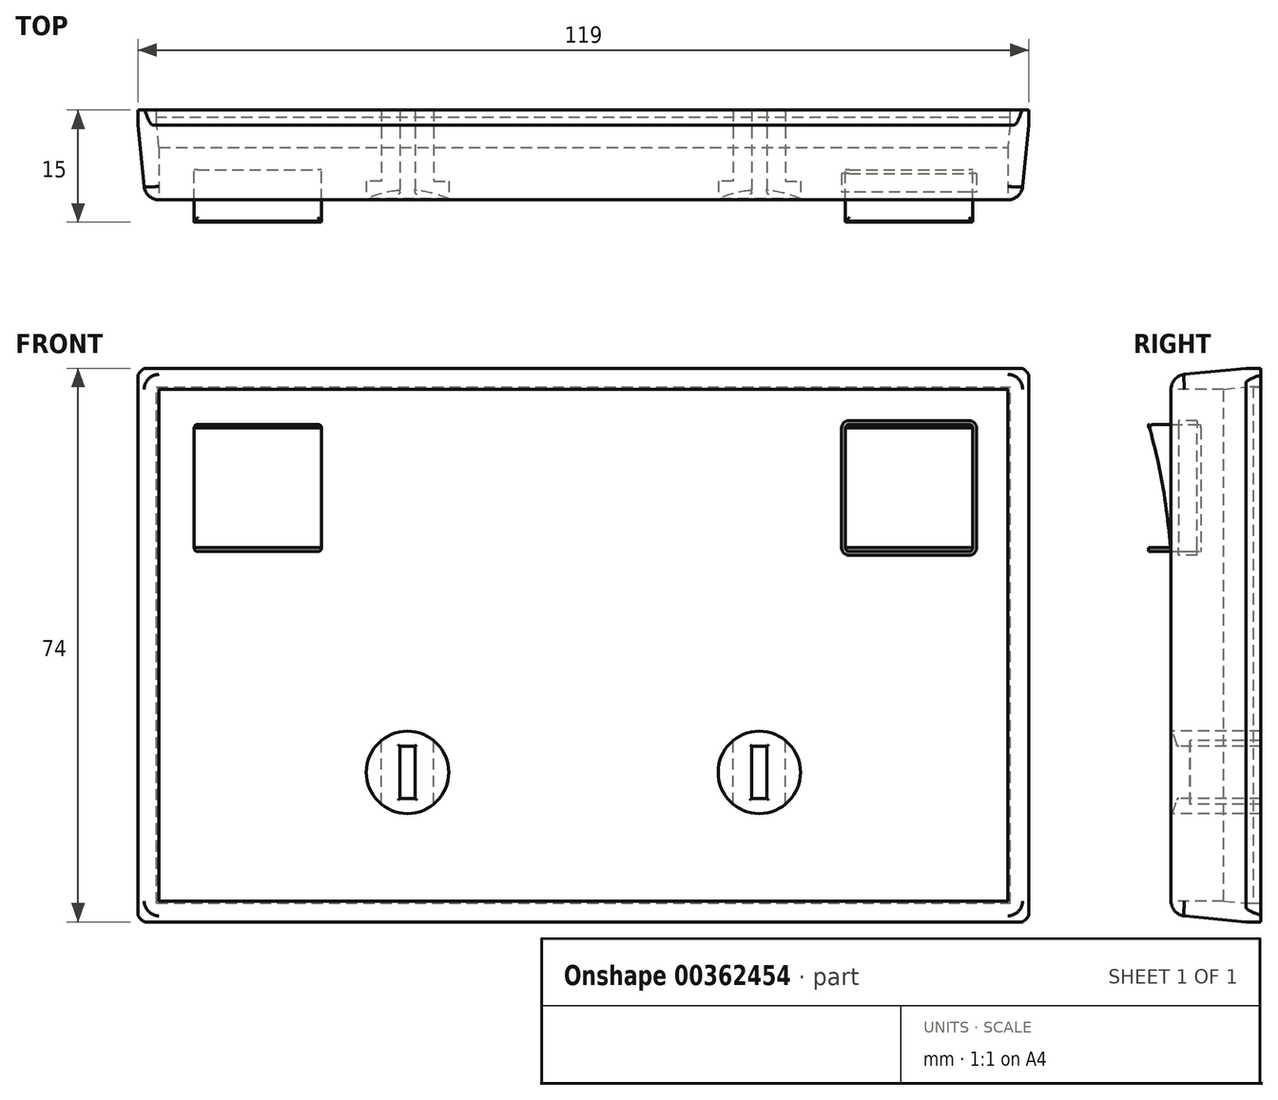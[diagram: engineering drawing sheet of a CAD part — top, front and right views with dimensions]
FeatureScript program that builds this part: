
annotation { "Feature Type Name" : "Feature", "Feature Type Description" : "" }
export const myFeature = defineFeature(function(context is Context, id is Id, definition is map)
    precondition{}
    {
        {
            var Q0;
            Q0=qCreatedBy(makeId("Front.planeOp"),FACE);
            var sketch = newSketch(context, id + "F0", { "sketchPlane" : qUnion([Q0])});
            skLineSegment(sketch, "E0.bottom", {"start": v(59.5, 37) * mm, "end": v(-59.5, 37) * mm});
            skLineSegment(sketch, "E0.top", {"start": v(59.5, -37) * mm, "end": v(-59.5, -37) * mm});
            skLineSegment(sketch, "E0.left", {"start": v(59.5, 37) * mm, "end": v(59.5, -37) * mm});
            skLineSegment(sketch, "E0.right", {"start": v(-59.5, 37) * mm, "end": v(-59.5, -37) * mm});
            skPoint(sketch, "E0.middle", {"position": v(0, 0) * mm});
            skSolve(sketch);
        }
        {
            var Q0;
            Q0=makeQuery(id+"F0.imprint","IMPRINT",FACE,{"disambiguationData":[TD([[makeQuery(id+"F0.imprint","IMPRINT",EDGE,{"derivedFrom":sQuery(id+"F0.wireOp",EDGE,"E0.bottom")}),1.0]])]});
            extrude(context, id + "F1", {"entities" : qUnion([Q0]), "depth" : 12 * mm});
        }
        {
            var Q0;
            Q0=makeQuery(id+"F1.opExtrude","CAP_EDGE",EDGE,{"disambiguationData":[OSD([sQuery(id+"F0.wireOp",EDGE,"E0.right")])],"isStart":false});
            var Q1;
            Q1=makeQuery(id+"F1.opExtrude","CAP_EDGE",EDGE,{"disambiguationData":[OSD([sQuery(id+"F0.wireOp",EDGE,"E0.bottom")])],"isStart":false});
            var Q2;
            Q2=makeQuery(id+"F1.opExtrude","CAP_EDGE",EDGE,{"disambiguationData":[OSD([sQuery(id+"F0.wireOp",EDGE,"E0.left")])],"isStart":false});
            var Q3;
            Q3=makeQuery(id+"F1.opExtrude","CAP_EDGE",EDGE,{"disambiguationData":[OSD([sQuery(id+"F0.wireOp",EDGE,"E0.top")])],"isStart":false});
            chamfer(context, id + "F2", {"entities" : qUnion([Q0, Q1, Q2, Q3]), "chamferType" : ChamferType.TWO_OFFSETS, "width1" : 1 * mm, "oppositeDirection" : false, "width2" : 10 * mm, "tangentPropagation" : true});
        }
        {
            var Q0;
            {var subQ0=sQuery(id+"F0.wireOp",EDGE,"E0.right");Q0=makeQuery(id+"F2.opChamfer","BLEND_EDGE",EDGE,{"blendedFrom":[makeQuery(id+"F1.opExtrude","CAP_EDGE",EDGE,{"disambiguationData":[OSD([subQ0])],"isStart":false}),makeQuery(id+"F1.opExtrude","CAP_FACE",FACE,{"disambiguationData":[OSD([sQuery(id+"F0.wireOp",EDGE,"E0.bottom"),sQuery(id+"F0.wireOp",EDGE,"E0.top"),sQuery(id+"F0.wireOp",EDGE,"E0.left"),subQ0])],"isStart":false})],"blendedInto":[makeQuery(id+"F1.opExtrude","CAP_FACE",FACE,{"disambiguationData":[OSD([sQuery(id+"F0.wireOp",EDGE,"E0.bottom"),sQuery(id+"F0.wireOp",EDGE,"E0.top"),sQuery(id+"F0.wireOp",EDGE,"E0.left"),subQ0])],"isStart":false})]});}
            var Q1;
            {var subQ0=sQuery(id+"F0.wireOp",EDGE,"E0.bottom");Q1=makeQuery(id+"F2.opChamfer","BLEND_EDGE",EDGE,{"blendedFrom":[makeQuery(id+"F1.opExtrude","CAP_EDGE",EDGE,{"disambiguationData":[OSD([subQ0])],"isStart":false}),makeQuery(id+"F1.opExtrude","CAP_FACE",FACE,{"disambiguationData":[OSD([subQ0,sQuery(id+"F0.wireOp",EDGE,"E0.top"),sQuery(id+"F0.wireOp",EDGE,"E0.left"),sQuery(id+"F0.wireOp",EDGE,"E0.right")])],"isStart":false})],"blendedInto":[makeQuery(id+"F1.opExtrude","CAP_FACE",FACE,{"disambiguationData":[OSD([subQ0,sQuery(id+"F0.wireOp",EDGE,"E0.top"),sQuery(id+"F0.wireOp",EDGE,"E0.left"),sQuery(id+"F0.wireOp",EDGE,"E0.right")])],"isStart":false})]});}
            var Q2;
            {var subQ0=sQuery(id+"F0.wireOp",EDGE,"E0.top");Q2=makeQuery(id+"F2.opChamfer","BLEND_EDGE",EDGE,{"blendedFrom":[makeQuery(id+"F1.opExtrude","CAP_EDGE",EDGE,{"disambiguationData":[OSD([subQ0])],"isStart":false}),makeQuery(id+"F1.opExtrude","CAP_FACE",FACE,{"disambiguationData":[OSD([sQuery(id+"F0.wireOp",EDGE,"E0.bottom"),subQ0,sQuery(id+"F0.wireOp",EDGE,"E0.left"),sQuery(id+"F0.wireOp",EDGE,"E0.right")])],"isStart":false})],"blendedInto":[makeQuery(id+"F1.opExtrude","CAP_FACE",FACE,{"disambiguationData":[OSD([sQuery(id+"F0.wireOp",EDGE,"E0.bottom"),subQ0,sQuery(id+"F0.wireOp",EDGE,"E0.left"),sQuery(id+"F0.wireOp",EDGE,"E0.right")])],"isStart":false})]});}
            var Q3;
            {var subQ0=sQuery(id+"F0.wireOp",EDGE,"E0.left");Q3=makeQuery(id+"F2.opChamfer","BLEND_EDGE",EDGE,{"blendedFrom":[makeQuery(id+"F1.opExtrude","CAP_EDGE",EDGE,{"disambiguationData":[OSD([subQ0])],"isStart":false}),makeQuery(id+"F1.opExtrude","CAP_FACE",FACE,{"disambiguationData":[OSD([sQuery(id+"F0.wireOp",EDGE,"E0.bottom"),sQuery(id+"F0.wireOp",EDGE,"E0.top"),subQ0,sQuery(id+"F0.wireOp",EDGE,"E0.right")])],"isStart":false})],"blendedInto":[makeQuery(id+"F1.opExtrude","CAP_FACE",FACE,{"disambiguationData":[OSD([sQuery(id+"F0.wireOp",EDGE,"E0.bottom"),sQuery(id+"F0.wireOp",EDGE,"E0.top"),subQ0,sQuery(id+"F0.wireOp",EDGE,"E0.right")])],"isStart":false})]});}
            fillet(context, id + "F3", {"entities" : qUnion([Q0, Q1, Q2, Q3]), "radius" : 2 * mm, "tangentPropagation" : true, "allowEdgeOverflow" : false});
        }
        {
            var Q0;
            Q0=makeQuery(id+"F2.opChamfer","BLEND_EDGE",EDGE,{"blendedFrom":[makeQuery(id+"F1.opExtrude","CAP_EDGE",EDGE,{"disambiguationData":[OSD([sQuery(id+"F0.wireOp",EDGE,"E0.bottom")])],"isStart":false}),makeQuery(id+"F1.opExtrude","CAP_EDGE",EDGE,{"disambiguationData":[OSD([sQuery(id+"F0.wireOp",EDGE,"E0.right")])],"isStart":false})],"blendedInto":[]});
            var Q1;
            Q1=makeQuery(id+"F2.opChamfer","BLEND_EDGE",EDGE,{"blendedFrom":[makeQuery(id+"F1.opExtrude","CAP_EDGE",EDGE,{"disambiguationData":[OSD([sQuery(id+"F0.wireOp",EDGE,"E0.top")])],"isStart":false}),makeQuery(id+"F1.opExtrude","CAP_EDGE",EDGE,{"disambiguationData":[OSD([sQuery(id+"F0.wireOp",EDGE,"E0.right")])],"isStart":false})],"blendedInto":[]});
            var Q2;
            Q2=makeQuery(id+"F2.opChamfer","BLEND_EDGE",EDGE,{"blendedFrom":[makeQuery(id+"F1.opExtrude","CAP_EDGE",EDGE,{"disambiguationData":[OSD([sQuery(id+"F0.wireOp",EDGE,"E0.top")])],"isStart":false}),makeQuery(id+"F1.opExtrude","CAP_EDGE",EDGE,{"disambiguationData":[OSD([sQuery(id+"F0.wireOp",EDGE,"E0.left")])],"isStart":false})],"blendedInto":[]});
            var Q3;
            Q3=makeQuery(id+"F2.opChamfer","BLEND_EDGE",EDGE,{"blendedFrom":[makeQuery(id+"F1.opExtrude","CAP_EDGE",EDGE,{"disambiguationData":[OSD([sQuery(id+"F0.wireOp",EDGE,"E0.bottom")])],"isStart":false}),makeQuery(id+"F1.opExtrude","CAP_EDGE",EDGE,{"disambiguationData":[OSD([sQuery(id+"F0.wireOp",EDGE,"E0.left")])],"isStart":false})],"blendedInto":[]});
            fillet(context, id + "F4", {"entities" : qUnion([Q0, Q1, Q2, Q3]), "radius" : 2 * mm, "tangentPropagation" : true, "allowEdgeOverflow" : false});
        }
        {
            var Q0;
            Q0=makeQuery(id+"F1.opExtrude","CAP_FACE",FACE,{"disambiguationData":[OSD([sQuery(id+"F0.wireOp",EDGE,"E0.bottom"),sQuery(id+"F0.wireOp",EDGE,"E0.top"),sQuery(id+"F0.wireOp",EDGE,"E0.left"),sQuery(id+"F0.wireOp",EDGE,"E0.right")])],"isStart":false});
            var sketch = newSketch(context, id + "F5", { "sketchPlane" : qUnion([Q0])});
            skLineSegment(sketch, "E1", {"start": v(0, 34.2) * mm, "end": v(0, -34.2) * mm, "construction": true});
            skLineSegment(sketch, "E2", {"start": v(-23.5, 34.2) * mm, "end": v(-23.5, -34.2) * mm, "construction": true});
            skPoint(sketch, "E3", {"position": v(-23.5, -17) * mm});
            skCircle(sketch, "E4", {"center": v(-23.5, -17) * mm, "radius": 5.5 * mm});
            skLineSegment(sketch, "E5.bottom", {"start": v(-22.5, -13.5) * mm, "end": v(-24.5, -13.5) * mm});
            skLineSegment(sketch, "E5.top", {"start": v(-22.5, -20.5) * mm, "end": v(-24.5, -20.5) * mm});
            skLineSegment(sketch, "E5.left", {"start": v(-22.5, -13.5) * mm, "end": v(-22.5, -20.5) * mm});
            skLineSegment(sketch, "E5.right", {"start": v(-24.5, -13.5) * mm, "end": v(-24.5, -20.5) * mm});
            skLineSegment(sketch, "E6", {"start": v(-56.7, -7.5) * mm, "end": v(56.7, -7.5) * mm, "construction": true});
            skPoint(sketch, "E7", {"position": v(-33.5, -7.5) * mm});
            skPoint(sketch, "E8", {"position": v(-13.5, -7.5) * mm});
            skLineSegment(sketch, "E9", {"start": v(-30, -34.2) * mm, "end": v(-30, 34.2) * mm, "construction": true});
            skLineSegment(sketch, "E10", {"start": v(-33.5, -7.5) * mm, "end": v(-30, -1.44) * mm});
            skLineSegment(sketch, "E11", {"start": v(-30, -1.44) * mm, "end": v(-28.27, -2.44) * mm});
            skLineSegment(sketch, "E12", {"start": v(-28.27, -2.44) * mm, "end": v(-31.77, -8.5) * mm});
            skLineSegment(sketch, "E13", {"start": v(-31.77, -8.5) * mm, "end": v(-33.5, -7.5) * mm});
            skLineSegment(sketch, "E14.MirrorCS", {"start": v(-15.23, -8.5) * mm, "end": v(-13.5, -7.5) * mm});
            skLineSegment(sketch, "E15.MirrorCS", {"start": v(-18.73, -2.44) * mm, "end": v(-15.23, -8.5) * mm});
            skLineSegment(sketch, "E16.MirrorCS", {"start": v(-13.5, -7.5) * mm, "end": v(-17, -1.44) * mm});
            skLineSegment(sketch, "E17.MirrorCS", {"start": v(-17, -1.44) * mm, "end": v(-18.73, -2.44) * mm});
            skCircle(sketch, "E18.MirrorC", {"center": v(23.5, -17) * mm, "radius": 5.5 * mm});
            skLineSegment(sketch, "E19.MirrorCS", {"start": v(22.5, -20.5) * mm, "end": v(24.5, -20.5) * mm});
            skLineSegment(sketch, "E20.MirrorCS", {"start": v(24.5, -13.5) * mm, "end": v(24.5, -20.5) * mm});
            skLineSegment(sketch, "E21.MirrorCS", {"start": v(22.5, -13.5) * mm, "end": v(24.5, -13.5) * mm});
            skLineSegment(sketch, "E22.MirrorCS", {"start": v(22.5, -13.5) * mm, "end": v(22.5, -20.5) * mm});
            skLineSegment(sketch, "E23.MirrorCS", {"start": v(15.23, -8.5) * mm, "end": v(13.5, -7.5) * mm});
            skLineSegment(sketch, "E24.MirrorCS", {"start": v(13.5, -7.5) * mm, "end": v(17, -1.44) * mm});
            skLineSegment(sketch, "E25.MirrorCS", {"start": v(17, -1.44) * mm, "end": v(18.73, -2.44) * mm});
            skLineSegment(sketch, "E26.MirrorCS", {"start": v(18.73, -2.44) * mm, "end": v(15.23, -8.5) * mm});
            skLineSegment(sketch, "E27.MirrorCS", {"start": v(31.77, -8.5) * mm, "end": v(33.5, -7.5) * mm});
            skLineSegment(sketch, "E28.MirrorCS", {"start": v(30, -1.44) * mm, "end": v(28.27, -2.44) * mm});
            skLineSegment(sketch, "E29.MirrorCS", {"start": v(33.5, -7.5) * mm, "end": v(30, -1.44) * mm});
            skLineSegment(sketch, "E30.MirrorCS", {"start": v(28.27, -2.44) * mm, "end": v(31.77, -8.5) * mm});
            skSolve(sketch);
        }
        {
            var Q0;
            Q0=makeQuery(id+"F5.imprint","IMPRINT",FACE,{"disambiguationData":[TD([[makeQuery(id+"F5.imprint","IMPRINT",EDGE,{"derivedFrom":sQuery(id+"F5.wireOp",EDGE,"E10")}),-1.0]])]});
            var Q1;
            Q1=makeQuery(id+"F5.imprint","IMPRINT",FACE,{"disambiguationData":[TD([[makeQuery(id+"F5.imprint","IMPRINT",EDGE,{"derivedFrom":sQuery(id+"F5.wireOp",EDGE,"E14.MirrorCS")}),1.0]])]});
            var Q2;
            Q2=makeQuery(id+"F5.imprint","IMPRINT",FACE,{"disambiguationData":[TD([[makeQuery(id+"F5.imprint","IMPRINT",EDGE,{"derivedFrom":sQuery(id+"F5.wireOp",EDGE,"E5.bottom")}),1.0]])]});
            var Q3;
            Q3=makeQuery(id+"F5.imprint","IMPRINT",FACE,{"disambiguationData":[TD([[makeQuery(id+"F5.imprint","IMPRINT",EDGE,{"derivedFrom":sQuery(id+"F5.wireOp",EDGE,"E23.MirrorCS")}),-1.0]])]});
            var Q4;
            Q4=makeQuery(id+"F5.imprint","IMPRINT",FACE,{"disambiguationData":[TD([[makeQuery(id+"F5.imprint","IMPRINT",EDGE,{"derivedFrom":sQuery(id+"F5.wireOp",EDGE,"E27.MirrorCS")}),1.0]])]});
            var Q5;
            Q5=makeQuery(id+"F5.imprint","IMPRINT",FACE,{"disambiguationData":[TD([[makeQuery(id+"F5.imprint","IMPRINT",EDGE,{"derivedFrom":sQuery(id+"F5.wireOp",EDGE,"E19.MirrorCS")}),1.0]])]});
            extrude(context, id + "F6", {"entities" : qUnion([Q0, Q1, Q2, Q3, Q4, Q5]), "operationType" : NewBodyOperationType.REMOVE, "endBound" : BoundingType.UP_TO_NEXT, "oppositeDirection" : true, "depth" : 25 * mm});
        }
        {
            var Q0;
            Q0=makeQuery(id+"F1.opExtrude","CAP_FACE",FACE,{"disambiguationData":[OSD([sQuery(id+"F0.wireOp",EDGE,"E0.bottom"),sQuery(id+"F0.wireOp",EDGE,"E0.top"),sQuery(id+"F0.wireOp",EDGE,"E0.left"),sQuery(id+"F0.wireOp",EDGE,"E0.right")])],"isStart":false});
            var sketch = newSketch(context, id + "F7", { "sketchPlane" : qUnion([Q0])});
            skLineSegment(sketch, "E31", {"start": v(-56.7, -10.5) * mm, "end": v(0, -10.5) * mm, "construction": true});
            skLineSegment(sketch, "E32.0", {"start": v(-23.5, 34.2) * mm, "end": v(-23.5, -34.2) * mm});
            skLineSegment(sketch, "E33.bottom", {"start": v(-11, 4.5) * mm, "end": v(-36, 4.5) * mm});
            skLineSegment(sketch, "E33.top", {"start": v(-11, -25.5) * mm, "end": v(-36, -25.5) * mm});
            skLineSegment(sketch, "E33.left", {"start": v(-8.5, 2) * mm, "end": v(-8.5, -23) * mm});
            skLineSegment(sketch, "E33.right", {"start": v(-38.5, 2) * mm, "end": v(-38.5, -23) * mm});
            skPoint(sketch, "E33.middle", {"position": v(-23.5, -10.5) * mm});
            skPoint(sketch, "E34.visualSharp", {"position": v(-38.5, 4.5) * mm});
            skArc(sketch, "E34.filletArc", {"start": v(-36, 4.5) * mm, "mid": v(-37.77, 3.77) * mm, "end": v(-38.5, 2) * mm});
            skPoint(sketch, "E35.visualSharp", {"position": v(-8.5, 4.5) * mm});
            skArc(sketch, "E35.filletArc", {"start": v(-8.5, 2) * mm, "mid": v(-9.23, 3.77) * mm, "end": v(-11, 4.5) * mm});
            skPoint(sketch, "E36.visualSharp", {"position": v(-8.5, -25.5) * mm});
            skArc(sketch, "E36.filletArc", {"start": v(-11, -25.5) * mm, "mid": v(-9.23, -24.77) * mm, "end": v(-8.5, -23) * mm});
            skPoint(sketch, "E37.visualSharp", {"position": v(-38.5, -25.5) * mm});
            skArc(sketch, "E37.filletArc", {"start": v(-38.5, -23) * mm, "mid": v(-37.77, -24.77) * mm, "end": v(-36, -25.5) * mm});
            skLineSegment(sketch, "E38.0", {"start": v(-11.1, 3.5) * mm, "end": v(-35.9, 3.5) * mm});
            skLineSegment(sketch, "E38.1", {"start": v(-9.5, 1.9) * mm, "end": v(-9.5, -22.9) * mm});
            skLineSegment(sketch, "E38.2", {"start": v(-11.1, -24.5) * mm, "end": v(-35.9, -24.5) * mm});
            skLineSegment(sketch, "E38.3", {"start": v(-37.5, 1.9) * mm, "end": v(-37.5, -22.9) * mm});
            skPoint(sketch, "E39.visualSharp", {"position": v(-37.5, 3.5) * mm});
            skArc(sketch, "E39.filletArc", {"start": v(-35.9, 3.5) * mm, "mid": v(-37.03, 3.03) * mm, "end": v(-37.5, 1.9) * mm});
            skPoint(sketch, "E40.visualSharp", {"position": v(-9.5, 3.5) * mm});
            skArc(sketch, "E40.filletArc", {"start": v(-9.5, 1.9) * mm, "mid": v(-9.97, 3.03) * mm, "end": v(-11.1, 3.5) * mm});
            skPoint(sketch, "E41.visualSharp", {"position": v(-9.5, -24.5) * mm});
            skArc(sketch, "E41.filletArc", {"start": v(-11.1, -24.5) * mm, "mid": v(-9.97, -24.03) * mm, "end": v(-9.5, -22.9) * mm});
            skPoint(sketch, "E42.visualSharp", {"position": v(-37.5, -24.5) * mm});
            skArc(sketch, "E42.filletArc", {"start": v(-37.5, -22.9) * mm, "mid": v(-37.03, -24.03) * mm, "end": v(-35.9, -24.5) * mm});
            skArc(sketch, "E43.MirrorCS", {"start": v(38.5, -23) * mm, "mid": v(37.77, -24.77) * mm, "end": v(36, -25.5) * mm});
            skArc(sketch, "E44.MirrorCS", {"start": v(37.5, -22.9) * mm, "mid": v(37.03, -24.03) * mm, "end": v(35.9, -24.5) * mm});
            skLineSegment(sketch, "E45.MirrorCS", {"start": v(11, -25.5) * mm, "end": v(36, -25.5) * mm});
            skLineSegment(sketch, "E46.MirrorCS", {"start": v(11.1, -24.5) * mm, "end": v(35.9, -24.5) * mm});
            skArc(sketch, "E47.MirrorCS", {"start": v(11.1, -24.5) * mm, "mid": v(9.97, -24.03) * mm, "end": v(9.5, -22.9) * mm});
            skArc(sketch, "E48.MirrorCS", {"start": v(11, -25.5) * mm, "mid": v(9.23, -24.77) * mm, "end": v(8.5, -23) * mm});
            skLineSegment(sketch, "E49.MirrorCS", {"start": v(8.5, 2) * mm, "end": v(8.5, -23) * mm});
            skLineSegment(sketch, "E50.MirrorCS", {"start": v(9.5, 1.9) * mm, "end": v(9.5, -22.9) * mm});
            skArc(sketch, "E51.MirrorCS", {"start": v(9.5, 1.9) * mm, "mid": v(9.97, 3.03) * mm, "end": v(11.1, 3.5) * mm});
            skArc(sketch, "E52.MirrorCS", {"start": v(8.5, 2) * mm, "mid": v(9.23, 3.77) * mm, "end": v(11, 4.5) * mm});
            skLineSegment(sketch, "E53.MirrorCS", {"start": v(37.5, 1.9) * mm, "end": v(37.5, -22.9) * mm});
            skLineSegment(sketch, "E54.MirrorCS", {"start": v(38.5, 2) * mm, "end": v(38.5, -23) * mm});
            skArc(sketch, "E55.MirrorCS", {"start": v(35.9, 3.5) * mm, "mid": v(37.03, 3.03) * mm, "end": v(37.5, 1.9) * mm});
            skArc(sketch, "E56.MirrorCS", {"start": v(36, 4.5) * mm, "mid": v(37.77, 3.77) * mm, "end": v(38.5, 2) * mm});
            skLineSegment(sketch, "E57.MirrorCS", {"start": v(11, 4.5) * mm, "end": v(36, 4.5) * mm});
            skLineSegment(sketch, "E58.MirrorCS", {"start": v(11.1, 3.5) * mm, "end": v(35.9, 3.5) * mm});
            skSolve(sketch);
        }
        {
            var Q0;
            Q0=makeQuery(id+"F7.imprint","IMPRINT",FACE,{"disambiguationData":[TD([[makeQuery(id+"F7.imprint","IMPRINT",EDGE,{"derivedFrom":sQuery(id+"F7.wireOp",EDGE,"E33.right")}),1.0]])]});
            var Q1;
            Q1=makeQuery(id+"F7.imprint","IMPRINT",FACE,{"disambiguationData":[TD([[makeQuery(id+"F7.imprint","IMPRINT",EDGE,{"derivedFrom":sQuery(id+"F7.wireOp",EDGE,"E33.left")}),-1.0]])]});
            var Q2;
            Q2=makeQuery(id+"F7.imprint","IMPRINT",FACE,{"disambiguationData":[TD([[makeQuery(id+"F7.imprint","IMPRINT",EDGE,{"derivedFrom":sQuery(id+"F7.wireOp",EDGE,"E43.MirrorCS")}),-1.0]])]});
            extrude(context, id + "F8", {"entities" : qUnion([Q0, Q1, Q2]), "operationType" : NewBodyOperationType.REMOVE, "oppositeDirection" : true, "depth" : 1 * mm});
        }
        {
            var Q0;
            Q0=makeQuery(id+"F5.imprint","IMPRINT",FACE,{"disambiguationData":[TD([[makeQuery(id+"F5.imprint","IMPRINT",EDGE,{"derivedFrom":sQuery(id+"F5.wireOp",EDGE,"E4")}),-1.0]])]});
            var sketch = newSketch(context, id + "F9", { "sketchPlane" : qUnion([Q0])});
            skLineSegment(sketch, "E59.bottom", {"start": v(-51.5, 30) * mm, "end": v(-35.5, 30) * mm});
            skLineSegment(sketch, "E59.top", {"start": v(-51.5, 12) * mm, "end": v(-35.5, 12) * mm});
            skLineSegment(sketch, "E59.left", {"start": v(-52.5, 29) * mm, "end": v(-52.5, 13) * mm});
            skLineSegment(sketch, "E59.right", {"start": v(-34.5, 29) * mm, "end": v(-34.5, 13) * mm});
            skPoint(sketch, "E60.visualSharp", {"position": v(-52.5, 30) * mm});
            skArc(sketch, "E60.filletArc", {"start": v(-51.5, 30) * mm, "mid": v(-52.2, 29.7) * mm, "end": v(-52.5, 29) * mm});
            skPoint(sketch, "E61.visualSharp", {"position": v(-34.5, 30) * mm});
            skArc(sketch, "E61.filletArc", {"start": v(-34.5, 29) * mm, "mid": v(-34.8, 29.7) * mm, "end": v(-35.5, 30) * mm});
            skPoint(sketch, "E62.visualSharp", {"position": v(-34.5, 12) * mm});
            skArc(sketch, "E62.filletArc", {"start": v(-35.5, 12) * mm, "mid": v(-34.8, 12.3) * mm, "end": v(-34.5, 13) * mm});
            skPoint(sketch, "E63.visualSharp", {"position": v(-52.5, 12) * mm});
            skArc(sketch, "E63.filletArc", {"start": v(-52.5, 13) * mm, "mid": v(-52.2, 12.3) * mm, "end": v(-51.5, 12) * mm});
            skArc(sketch, "E64.MirrorCS", {"start": v(34.5, 29) * mm, "mid": v(34.8, 29.7) * mm, "end": v(35.5, 30) * mm});
            skLineSegment(sketch, "E65.MirrorCS", {"start": v(34.5, 29) * mm, "end": v(34.5, 13) * mm});
            skArc(sketch, "E66.MirrorCS", {"start": v(35.5, 12) * mm, "mid": v(34.8, 12.3) * mm, "end": v(34.5, 13) * mm});
            skLineSegment(sketch, "E67.MirrorCS", {"start": v(51.5, 12) * mm, "end": v(35.5, 12) * mm});
            skArc(sketch, "E68.MirrorCS", {"start": v(52.5, 13) * mm, "mid": v(52.2, 12.3) * mm, "end": v(51.5, 12) * mm});
            skLineSegment(sketch, "E69.MirrorCS", {"start": v(51.5, 30) * mm, "end": v(35.5, 30) * mm});
            skLineSegment(sketch, "E70.MirrorCS", {"start": v(52.5, 29) * mm, "end": v(52.5, 13) * mm});
            skArc(sketch, "E71.MirrorCS", {"start": v(51.5, 30) * mm, "mid": v(52.2, 29.7) * mm, "end": v(52.5, 29) * mm});
            skSolve(sketch);
        }
        {
            var Q0;
            Q0=makeQuery(id+"F9.imprint","IMPRINT",FACE,{"disambiguationData":[TD([[makeQuery(id+"F9.imprint","IMPRINT",EDGE,{"derivedFrom":sQuery(id+"F9.wireOp",EDGE,"E59.bottom")}),-1.0]])]});
            extrude(context, id + "F10", {"entities" : qUnion([Q0]), "operationType" : NewBodyOperationType.REMOVE, "endBound" : BoundingType.UP_TO_NEXT, "oppositeDirection" : true, "depth" : 25 * mm});
        }
        {
            var Q0;
            Q0=makeQuery(id+"F1.opExtrude","CAP_FACE",FACE,{"disambiguationData":[OSD([sQuery(id+"F0.wireOp",EDGE,"E0.bottom"),sQuery(id+"F0.wireOp",EDGE,"E0.top"),sQuery(id+"F0.wireOp",EDGE,"E0.left"),sQuery(id+"F0.wireOp",EDGE,"E0.right")])],"isStart":true});
            shell(context, id + "F11", {"entities" : qUnion([Q0]), "thickness" : 2.5 * mm});
        }
        {
            var Q0;
            Q0=makeQuery(id+"F5.imprint","IMPRINT",FACE,{"disambiguationData":[TD([[makeQuery(id+"F5.imprint","IMPRINT",EDGE,{"derivedFrom":sQuery(id+"F5.wireOp",EDGE,"E4")}),-1.0]])]});
            var sketch = newSketch(context, id + "F12", { "sketchPlane" : qUnion([Q0])});
            skLineSegment(sketch, "E72.0", {"start": v(-51.5, 30) * mm, "end": v(-35.5, 30) * mm});
            skLineSegment(sketch, "E73.0", {"start": v(-34.5, 29) * mm, "end": v(-34.5, 13) * mm});
            skLineSegment(sketch, "E74.0", {"start": v(-51.5, 12) * mm, "end": v(-35.5, 12) * mm});
            skLineSegment(sketch, "E75.0", {"start": v(-52.5, 29) * mm, "end": v(-52.5, 13) * mm});
            skLineSegment(sketch, "E76.0", {"start": v(-51.5, 29.5) * mm, "end": v(-35.5, 29.5) * mm});
            skLineSegment(sketch, "E77.0", {"start": v(-52, 29) * mm, "end": v(-52, 13) * mm});
            skLineSegment(sketch, "E78.0", {"start": v(-51.5, 12.5) * mm, "end": v(-35.5, 12.5) * mm});
            skLineSegment(sketch, "E79.0", {"start": v(-35, 29) * mm, "end": v(-35, 13) * mm});
            skArc(sketch, "E80.filletArc", {"start": v(-51.5, 29.5) * mm, "mid": v(-51.85, 29.35) * mm, "end": v(-52, 29) * mm});
            skArc(sketch, "E81.filletArc", {"start": v(-35, 29) * mm, "mid": v(-35.15, 29.35) * mm, "end": v(-35.5, 29.5) * mm});
            skArc(sketch, "E82.filletArc", {"start": v(-35.5, 12.5) * mm, "mid": v(-35.15, 12.65) * mm, "end": v(-35, 13) * mm});
            skArc(sketch, "E83.filletArc", {"start": v(-52, 13) * mm, "mid": v(-51.85, 12.65) * mm, "end": v(-51.5, 12.5) * mm});
            skSolve(sketch);
        }
        {
            var Q0;
            Q0=makeQuery(id+"F12.imprint","IMPRINT",FACE,{"disambiguationData":[TD([[makeQuery(id+"F12.imprint","IMPRINT",EDGE,{"derivedFrom":sQuery(id+"F12.wireOp",EDGE,"E76.0")}),-1.0]])]});
            extrude(context, id + "F13", {"entities" : qUnion([Q0]), "depth" : 3 * mm, "hasSecondDirection" : true, "secondDirectionOppositeDirection" : true, "secondDirectionDepth" : 4 * mm});
        }
        {
            var Q0;
            Q0=makeQuery(id+"F13.opExtrude","SWEPT_FACE",FACE,{"disambiguationData":[OSD([sQuery(id+"F12.wireOp",EDGE,"E77.0")])]});
            var sketch = newSketch(context, id + "F14", { "sketchPlane" : qUnion([Q0])});
            skLineSegment(sketch, "E84.0", {"start": v(14.34, 29.5) * mm, "end": v(8, 29.5) * mm});
            skLineSegment(sketch, "E85.0", {"start": v(15, 12.5) * mm, "end": v(8, 12.5) * mm});
            skFitSpline(sketch, "E86", {"points": [v(15, 29.5) * mm, v(12.06, 12.5) * mm], "startDerivative": vector(-4.71, -17) * mm, "endDerivative": vector(-1.43, -19.4) * mm});
            skArc(sketch, "E87.filletArc", {"start": v(14.83, 28.87) * mm, "mid": v(14.74, 29.3) * mm, "end": v(14.34, 29.5) * mm});
            skLineSegment(sketch, "E88", {"start": v(14.34, 29.5) * mm, "end": v(15, 29.5) * mm});
            skLineSegment(sketch, "E89", {"start": v(15, 29.5) * mm, "end": v(15, 12.5) * mm});
            skLineSegment(sketch, "E90", {"start": v(15, 12.5) * mm, "end": v(12.06, 12.5) * mm});
            skSolve(sketch);
        }
        {
            var Q0;
            {var subQ4=sQuery(id+"F14.wireOp",EDGE,"E87.filletArc");var subQ6=sQuery(id+"F14.wireOp",EDGE,"E86");var subQ7=makeQuery(id+"F14.imprint","INTERSECT",VERTEX,{"derivedFrom":[subQ6,subQ4]});Q0=makeQuery(id+"F14.imprint","IMPRINT",FACE,{"disambiguationData":[TD([[makeQuery(id+"F14.imprint","IMPRINT",EDGE,{"disambiguationData":[TD([[subQ7,-1.0]])],"derivedFrom":subQ6}),1.0]])]});}
            var Q1;
            {var subQ0=sQuery(id+"F14.wireOp",EDGE,"E88");Q1=makeQuery(id+"F14.imprint","IMPRINT",FACE,{"disambiguationData":[TD([[makeQuery(id+"F14.imprint","IMPRINT",EDGE,{"derivedFrom":subQ0}),-1.0]])]});}
            var Q2;
            {var subQ0=sQuery(id+"F14.wireOp",EDGE,"E90");Q2=makeQuery(id+"F14.imprint","IMPRINT",FACE,{"disambiguationData":[TD([[makeQuery(id+"F14.imprint","IMPRINT",EDGE,{"derivedFrom":subQ0}),-1.0]])]});}
            var Q3;
            Q3=makeQuery(id+"F13.opExtrude","SWEPT_FACE",FACE,{"disambiguationData":[OSD([sQuery(id+"F12.wireOp",EDGE,"E79.0")])]});
            extrude(context, id + "F15", {"entities" : qUnion([Q0, Q1, Q2]), "operationType" : NewBodyOperationType.REMOVE, "endBound" : BoundingType.UP_TO_SURFACE, "oppositeDirection" : true, "endBoundEntityFace" : qUnion([Q3]), "depth" : 25 * mm});
        }
        {
            var Q0;
            Q0=makeQuery(id+"F9.imprint","IMPRINT",FACE,{"disambiguationData":[TD([[makeQuery(id+"F9.imprint","IMPRINT",EDGE,{"derivedFrom":sQuery(id+"F9.wireOp",EDGE,"E64.MirrorCS")}),-1.0]])]});
            extrude(context, id + "F16", {"entities" : qUnion([Q0]), "operationType" : NewBodyOperationType.REMOVE, "endBound" : BoundingType.UP_TO_NEXT, "oppositeDirection" : true, "depth" : 25 * mm});
        }
        {
            var Q0;
            Q0=makeQuery(id+"F13.opExtrude","SWEPT_BODY",BODY,{"disambiguationData":[OSD([sQuery(id+"F12.wireOp",EDGE,"E76.0"),sQuery(id+"F12.wireOp",EDGE,"E77.0"),sQuery(id+"F12.wireOp",EDGE,"E78.0"),sQuery(id+"F12.wireOp",EDGE,"E79.0"),sQuery(id+"F12.wireOp",EDGE,"E80.filletArc"),sQuery(id+"F12.wireOp",EDGE,"E81.filletArc"),sQuery(id+"F12.wireOp",EDGE,"E82.filletArc"),sQuery(id+"F12.wireOp",EDGE,"E83.filletArc")])]});
            transform(context, id + "F17", {"entities" : qUnion([Q0]), "transformType" : TransformType.TRANSLATION_3D, "dx" : 87 * mm, "dy" : 0 * mm, "dz" : 0 * mm, "makeCopy" : true});
        }
        {
            var Q0;
            Q0=makeQuery(id+"F5.imprint","IMPRINT",FACE,{"disambiguationData":[TD([[makeQuery(id+"F5.imprint","IMPRINT",EDGE,{"derivedFrom":sQuery(id+"F5.wireOp",EDGE,"E4")}),-1.0]])]});
            cPlane(context, id + "F18", {"entities" : qUnion([Q0]), "cplaneType" : CPlaneType.OFFSET, "offset" : 12.2 * mm, "width" : 150 * mm, "height" : 150 * mm});
        }
        {
            var Q0;
            Q0=qCreatedBy(id+"F18.planeOp",FACE);
            var sketch = newSketch(context, id + "F19", { "sketchPlane" : qUnion([Q0])});
            skPoint(sketch, "E91.0", {"position": v(-23.5, -17) * mm});
            skArc(sketch, "E92.0", {"start": v(-23.5, -11.5) * mm, "mid": v(-29, -17) * mm, "end": v(-23.5, -22.5) * mm});
            skArc(sketch, "E93", {"start": v(-23.5, -3.5) * mm, "mid": v(-37, -17) * mm, "end": v(-23.5, -30.5) * mm});
            skLineSegment(sketch, "E94", {"start": v(-23.5, -17) * mm, "end": v(-23.5, -3.5) * mm});
            skLineSegment(sketch, "E95", {"start": v(-23.5, -17) * mm, "end": v(-23.5, -30.5) * mm});
            skLineSegment(sketch, "E96.MirrorCS", {"start": v(23.5, -17) * mm, "end": v(23.5, -3.5) * mm});
            skLineSegment(sketch, "E97.MirrorCS", {"start": v(23.5, -17) * mm, "end": v(23.5, -30.5) * mm});
            skArc(sketch, "E98.MirrorCS", {"start": v(23.5, -3.5) * mm, "mid": v(37, -17) * mm, "end": v(23.5, -30.5) * mm});
            skSolve(sketch);
        }
        {
            var Q0;
            {var subQ0=sQuery(id+"F19.wireOp",EDGE,"E92.0");Q0=makeQuery(id+"F19.imprint","IMPRINT",FACE,{"disambiguationData":[TD([[makeQuery(id+"F19.imprint","IMPRINT",EDGE,{"derivedFrom":subQ0}),-1.0]])]});}
            var Q1;
            Q1=sQuery(id+"F19.wireOp",EDGE,"E94");
            revolve(context, id + "F20", {"operationType" : NewBodyOperationType.REMOVE, "entities" : qUnion([Q0]), "axis" : qUnion([Q1]), "revolveType" : RevolveType.FULL, "oppositeDirection" : true});
        }
        {
            var Q0;
            Q0=makeQuery(id+"F19.imprint","IMPRINT",FACE,{"disambiguationData":[TD([[makeQuery(id+"F19.imprint","IMPRINT",EDGE,{"derivedFrom":sQuery(id+"F19.wireOp",EDGE,"E96.MirrorCS")}),-1.0]])]});
            var Q1;
            Q1=sQuery(id+"F19.wireOp",EDGE,"E96.MirrorCS");
            revolve(context, id + "F21", {"operationType" : NewBodyOperationType.REMOVE, "entities" : qUnion([Q0]), "axis" : qUnion([Q1]), "revolveType" : RevolveType.FULL, "oppositeDirection" : true});
        }
        {
            var Q0;
            {var subQ0=sQuery(id+"F0.wireOp",EDGE,"E0.right");var subQ1=sQuery(id+"F0.wireOp",EDGE,"E0.left");var subQ2=sQuery(id+"F0.wireOp",EDGE,"E0.top");var subQ3=sQuery(id+"F0.wireOp",EDGE,"E0.bottom");Q0=makeQuery(id+"F11.opShell","OFFSET_FACE",FACE,{"disambiguationData":[OSD([subQ3,subQ2,subQ1,subQ0]),TDD([makeQuery(id+"F1.opExtrude","CAP_FACE",FACE,{"disambiguationData":[OSD([subQ3,subQ2,subQ1,subQ0])],"isStart":true})]),OD(0.0)]});}
            var sketch = newSketch(context, id + "F22", { "sketchPlane" : qUnion([Q0])});
            skLineSegment(sketch, "E99.bottom", {"start": v(-57, 34.5) * mm, "end": v(57, 34.5) * mm});
            skLineSegment(sketch, "E99.top", {"start": v(-57, -34.5) * mm, "end": v(57, -34.5) * mm});
            skLineSegment(sketch, "E99.left", {"start": v(-57, 34.5) * mm, "end": v(-57, -34.5) * mm});
            skLineSegment(sketch, "E99.right", {"start": v(57, 34.5) * mm, "end": v(57, -34.5) * mm});
            skSolve(sketch);
        }
        {
            var Q0;
            Q0=makeQuery(id+"F22.imprint","IMPRINT",FACE,{"disambiguationData":[TD([[makeQuery(id+"F22.imprint","IMPRINT",EDGE,{"derivedFrom":sQuery(id+"F22.wireOp",EDGE,"E99.bottom")}),-1.0]])]});
            extrude(context, id + "F23", {"entities" : qUnion([Q0]), "oppositeDirection" : true, "depth" : 1 * mm});
        }
        {
            var Q0;
            Q0=makeQuery(id+"F6.boolean.opBoolean","COPY",EDGE,{"derivedFrom":makeQuery(id+"F6.opExtrude","CAP_EDGE",EDGE,{"disambiguationData":[OSD([sQuery(id+"F5.wireOp",EDGE,"E10")])],"isStart":true})});
            var Q1;
            Q1=makeQuery(id+"F6.boolean.opBoolean","COPY",EDGE,{"derivedFrom":makeQuery(id+"F6.opExtrude","CAP_EDGE",EDGE,{"disambiguationData":[OSD([sQuery(id+"F5.wireOp",EDGE,"E12")])],"isStart":true})});
            var Q2;
            Q2=makeQuery(id+"F6.boolean.opBoolean","COPY",EDGE,{"derivedFrom":makeQuery(id+"F6.opExtrude","CAP_EDGE",EDGE,{"disambiguationData":[OSD([sQuery(id+"F5.wireOp",EDGE,"E11")])],"isStart":true})});
            var Q3;
            Q3=makeQuery(id+"F6.boolean.opBoolean","COPY",EDGE,{"derivedFrom":makeQuery(id+"F6.opExtrude","CAP_EDGE",EDGE,{"disambiguationData":[OSD([sQuery(id+"F5.wireOp",EDGE,"E13")])],"isStart":true})});
            var Q4;
            Q4=makeQuery(id+"F6.boolean.opBoolean","COPY",EDGE,{"derivedFrom":makeQuery(id+"F6.opExtrude","CAP_EDGE",EDGE,{"disambiguationData":[OSD([sQuery(id+"F5.wireOp",EDGE,"E15.MirrorCS")])],"isStart":true})});
            var Q5;
            Q5=makeQuery(id+"F6.boolean.opBoolean","COPY",EDGE,{"derivedFrom":makeQuery(id+"F6.opExtrude","CAP_EDGE",EDGE,{"disambiguationData":[OSD([sQuery(id+"F5.wireOp",EDGE,"E16.MirrorCS")])],"isStart":true})});
            var Q6;
            Q6=makeQuery(id+"F6.boolean.opBoolean","COPY",EDGE,{"derivedFrom":makeQuery(id+"F6.opExtrude","CAP_EDGE",EDGE,{"disambiguationData":[OSD([sQuery(id+"F5.wireOp",EDGE,"E17.MirrorCS")])],"isStart":true})});
            var Q7;
            Q7=makeQuery(id+"F6.boolean.opBoolean","COPY",EDGE,{"derivedFrom":makeQuery(id+"F6.opExtrude","CAP_EDGE",EDGE,{"disambiguationData":[OSD([sQuery(id+"F5.wireOp",EDGE,"E14.MirrorCS")])],"isStart":true})});
            var Q8;
            Q8=makeQuery(id+"F20.boolean.opBoolean","INTERSECT",EDGE,{"derivedFrom":[makeQuery(id+"F6.boolean.opBoolean","COPY",FACE,{"derivedFrom":makeQuery(id+"F6.opExtrude","SWEPT_FACE",FACE,{"disambiguationData":[OSD([sQuery(id+"F5.wireOp",EDGE,"E5.left")])]})}),makeQuery(id+"F20.opRevolve","SWEPT_FACE",FACE,{"disambiguationData":[OSD([sQuery(id+"F19.wireOp",EDGE,"E93")])]})]});
            var Q9;
            Q9=makeQuery(id+"F20.boolean.opBoolean","INTERSECT",EDGE,{"derivedFrom":[makeQuery(id+"F6.boolean.opBoolean","COPY",FACE,{"derivedFrom":makeQuery(id+"F6.opExtrude","SWEPT_FACE",FACE,{"disambiguationData":[OSD([sQuery(id+"F5.wireOp",EDGE,"E5.right")])]})}),makeQuery(id+"F20.opRevolve","SWEPT_FACE",FACE,{"disambiguationData":[OSD([sQuery(id+"F19.wireOp",EDGE,"E93")])]})]});
            var Q10;
            Q10=makeQuery(id+"F20.boolean.opBoolean","INTERSECT",EDGE,{"derivedFrom":[makeQuery(id+"F6.boolean.opBoolean","COPY",FACE,{"derivedFrom":makeQuery(id+"F6.opExtrude","SWEPT_FACE",FACE,{"disambiguationData":[OSD([sQuery(id+"F5.wireOp",EDGE,"E5.bottom")])]})}),makeQuery(id+"F20.opRevolve","SWEPT_FACE",FACE,{"disambiguationData":[OSD([sQuery(id+"F19.wireOp",EDGE,"E93")])]})]});
            var Q11;
            Q11=makeQuery(id+"F20.boolean.opBoolean","INTERSECT",EDGE,{"derivedFrom":[makeQuery(id+"F6.boolean.opBoolean","COPY",FACE,{"derivedFrom":makeQuery(id+"F6.opExtrude","SWEPT_FACE",FACE,{"disambiguationData":[OSD([sQuery(id+"F5.wireOp",EDGE,"E5.top")])]})}),makeQuery(id+"F20.opRevolve","SWEPT_FACE",FACE,{"disambiguationData":[OSD([sQuery(id+"F19.wireOp",EDGE,"E93")])]})]});
            var Q12;
            Q12=makeQuery(id+"F21.boolean.opBoolean","INTERSECT",EDGE,{"derivedFrom":[makeQuery(id+"F6.boolean.opBoolean","COPY",FACE,{"derivedFrom":makeQuery(id+"F6.opExtrude","SWEPT_FACE",FACE,{"disambiguationData":[OSD([sQuery(id+"F5.wireOp",EDGE,"E22.MirrorCS")])]})}),makeQuery(id+"F21.opRevolve","SWEPT_FACE",FACE,{"disambiguationData":[OSD([sQuery(id+"F19.wireOp",EDGE,"E98.MirrorCS")])]})]});
            var Q13;
            Q13=makeQuery(id+"F21.boolean.opBoolean","INTERSECT",EDGE,{"derivedFrom":[makeQuery(id+"F6.boolean.opBoolean","COPY",FACE,{"derivedFrom":makeQuery(id+"F6.opExtrude","SWEPT_FACE",FACE,{"disambiguationData":[OSD([sQuery(id+"F5.wireOp",EDGE,"E20.MirrorCS")])]})}),makeQuery(id+"F21.opRevolve","SWEPT_FACE",FACE,{"disambiguationData":[OSD([sQuery(id+"F19.wireOp",EDGE,"E98.MirrorCS")])]})]});
            var Q14;
            Q14=makeQuery(id+"F21.boolean.opBoolean","INTERSECT",EDGE,{"derivedFrom":[makeQuery(id+"F6.boolean.opBoolean","COPY",FACE,{"derivedFrom":makeQuery(id+"F6.opExtrude","SWEPT_FACE",FACE,{"disambiguationData":[OSD([sQuery(id+"F5.wireOp",EDGE,"E21.MirrorCS")])]})}),makeQuery(id+"F21.opRevolve","SWEPT_FACE",FACE,{"disambiguationData":[OSD([sQuery(id+"F19.wireOp",EDGE,"E98.MirrorCS")])]})]});
            var Q15;
            Q15=makeQuery(id+"F21.boolean.opBoolean","INTERSECT",EDGE,{"derivedFrom":[makeQuery(id+"F6.boolean.opBoolean","COPY",FACE,{"derivedFrom":makeQuery(id+"F6.opExtrude","SWEPT_FACE",FACE,{"disambiguationData":[OSD([sQuery(id+"F5.wireOp",EDGE,"E19.MirrorCS")])]})}),makeQuery(id+"F21.opRevolve","SWEPT_FACE",FACE,{"disambiguationData":[OSD([sQuery(id+"F19.wireOp",EDGE,"E98.MirrorCS")])]})]});
            var Q16;
            Q16=makeQuery(id+"F6.boolean.opBoolean","COPY",EDGE,{"derivedFrom":makeQuery(id+"F6.opExtrude","CAP_EDGE",EDGE,{"disambiguationData":[OSD([sQuery(id+"F5.wireOp",EDGE,"E23.MirrorCS")])],"isStart":true})});
            var Q17;
            Q17=makeQuery(id+"F6.boolean.opBoolean","COPY",EDGE,{"derivedFrom":makeQuery(id+"F6.opExtrude","CAP_EDGE",EDGE,{"disambiguationData":[OSD([sQuery(id+"F5.wireOp",EDGE,"E24.MirrorCS")])],"isStart":true})});
            var Q18;
            Q18=makeQuery(id+"F6.boolean.opBoolean","COPY",EDGE,{"derivedFrom":makeQuery(id+"F6.opExtrude","CAP_EDGE",EDGE,{"disambiguationData":[OSD([sQuery(id+"F5.wireOp",EDGE,"E26.MirrorCS")])],"isStart":true})});
            var Q19;
            Q19=makeQuery(id+"F6.boolean.opBoolean","COPY",EDGE,{"derivedFrom":makeQuery(id+"F6.opExtrude","CAP_EDGE",EDGE,{"disambiguationData":[OSD([sQuery(id+"F5.wireOp",EDGE,"E25.MirrorCS")])],"isStart":true})});
            var Q20;
            Q20=makeQuery(id+"F6.boolean.opBoolean","COPY",EDGE,{"derivedFrom":makeQuery(id+"F6.opExtrude","CAP_EDGE",EDGE,{"disambiguationData":[OSD([sQuery(id+"F5.wireOp",EDGE,"E30.MirrorCS")])],"isStart":true})});
            var Q21;
            Q21=makeQuery(id+"F6.boolean.opBoolean","COPY",EDGE,{"derivedFrom":makeQuery(id+"F6.opExtrude","CAP_EDGE",EDGE,{"disambiguationData":[OSD([sQuery(id+"F5.wireOp",EDGE,"E29.MirrorCS")])],"isStart":true})});
            var Q22;
            Q22=makeQuery(id+"F6.boolean.opBoolean","COPY",EDGE,{"derivedFrom":makeQuery(id+"F6.opExtrude","CAP_EDGE",EDGE,{"disambiguationData":[OSD([sQuery(id+"F5.wireOp",EDGE,"E28.MirrorCS")])],"isStart":true})});
            var Q23;
            Q23=makeQuery(id+"F6.boolean.opBoolean","COPY",EDGE,{"derivedFrom":makeQuery(id+"F6.opExtrude","CAP_EDGE",EDGE,{"disambiguationData":[OSD([sQuery(id+"F5.wireOp",EDGE,"E27.MirrorCS")])],"isStart":true})});
            fillet(context, id + "F24", {"entities" : qUnion([Q0, Q1, Q2, Q3, Q4, Q5, Q6, Q7, Q8, Q9, Q10, Q11, Q12, Q13, Q14, Q15, Q16, Q17, Q18, Q19, Q20, Q21, Q22, Q23]), "radius" : .25 * mm, "tangentPropagation" : true, "allowEdgeOverflow" : false});
        }
    });
